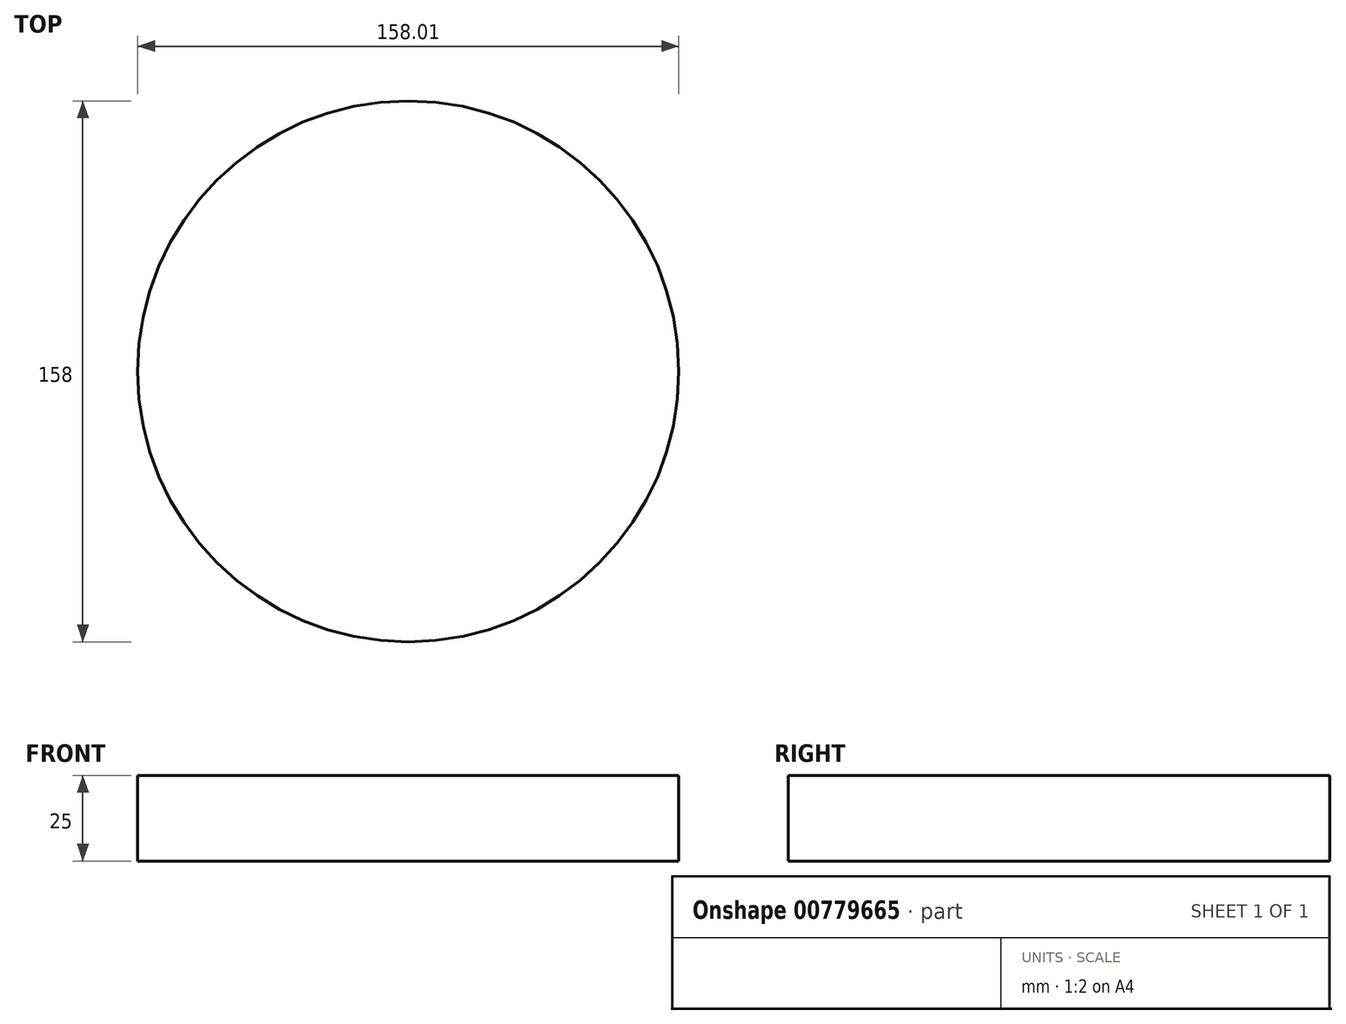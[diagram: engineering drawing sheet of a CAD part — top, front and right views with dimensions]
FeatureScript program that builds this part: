
annotation { "Feature Type Name" : "Feature", "Feature Type Description" : "" }
export const myFeature = defineFeature(function(context is Context, id is Id, definition is map)
    precondition{}
    {
        {
            var Q0;
            Q0=qCreatedBy(makeId("Top.planeOp"),FACE);
            var sketch = newSketch(context, id + "F0", { "sketchPlane" : qUnion([Q0])});
            skCircle(sketch, "E0", {"center": v(5.18, -7.65) * mm, "radius": 79 * mm});
            skSolve(sketch);
        }
        {
            var Q0;
            Q0=makeQuery(id+"F0.imprint","IMPRINT",FACE,{"disambiguationData":[TD([[makeQuery(id+"F0.imprint","IMPRINT",EDGE,{"derivedFrom":sQuery(id+"F0.wireOp",EDGE,"E0")}),1.0]])]});
            extrude(context, id + "F1", {"entities" : qUnion([Q0]), "depth" : 25 * mm, "offsetDistance" : 25 * mm});
        }
    });
